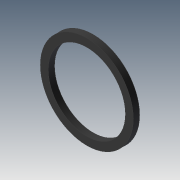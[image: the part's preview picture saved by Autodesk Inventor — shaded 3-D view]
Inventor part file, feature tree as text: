
AUTODESK INVENTOR PART (.ipt)
format: ipt  version: 2020 (Build 240168000, 168)  size: 85,504 bytes
history: native  units: mm
features: extrude x1, sketch x1
ambient origin geometry x8: Origin, YZ Plane, XZ Plane, XY Plane, X Axis, Y Axis, Z Axis, Center Point
bodies: Solid1 (feature_tree)
feature tree (2):
  extrude  "Extrusion1"  Depth=3.0mm
  sketch  "Sketch1"  dims[d0=36.5mm d1=44.0mm d2=3.0mm d3=0.0mm]
